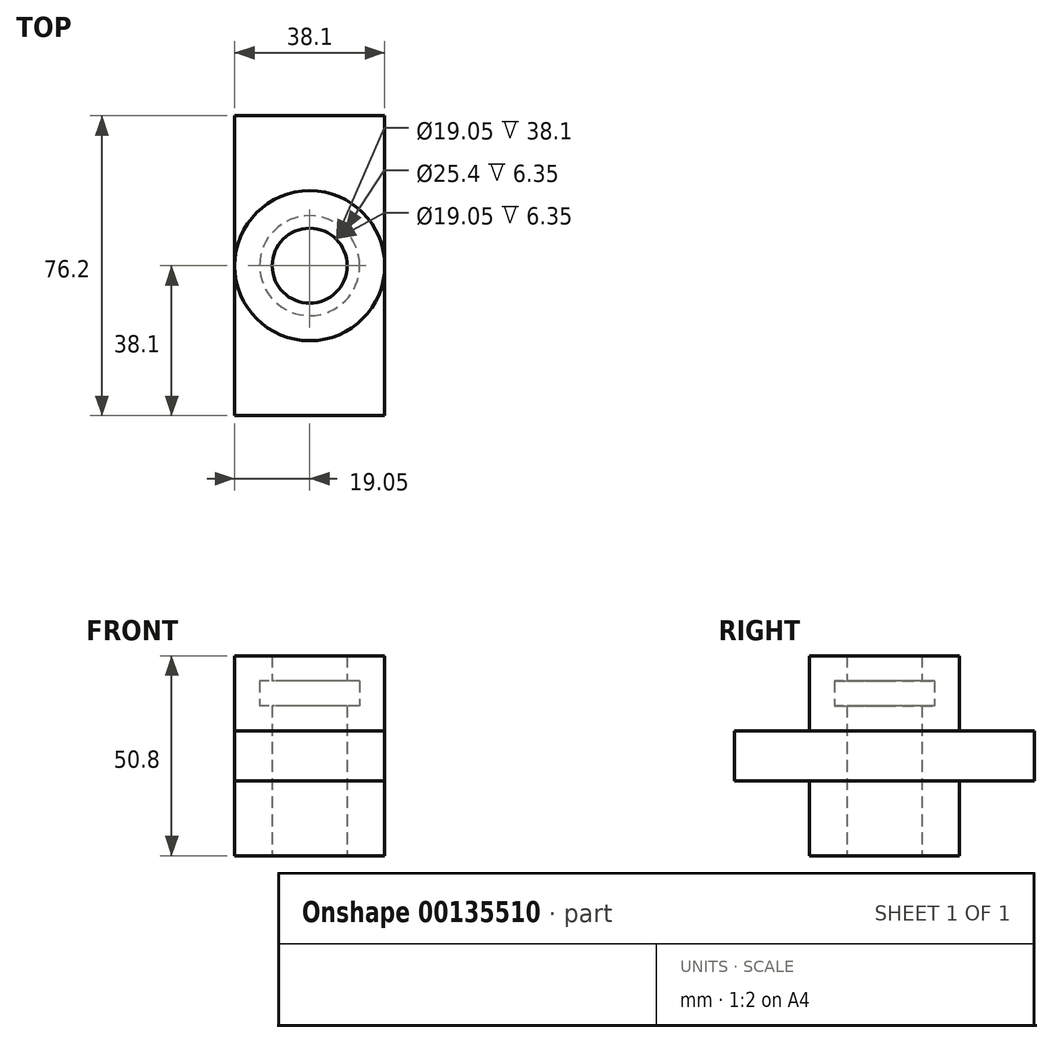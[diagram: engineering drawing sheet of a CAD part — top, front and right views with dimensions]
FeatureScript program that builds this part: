
annotation { "Feature Type Name" : "Feature", "Feature Type Description" : "" }
export const myFeature = defineFeature(function(context is Context, id is Id, definition is map)
    precondition{}
    {
        {
            var Q0;
            Q0=qCreatedBy(makeId("Top.planeOp"),FACE);
            var sketch = newSketch(context, id + "F0", { "sketchPlane" : qUnion([Q0])});
            skCircle(sketch, "E0", {"center": v(0, 0) * mm, "radius": 19.05 * mm});
            skCircle(sketch, "E1", {"center": v(0, 0) * mm, "radius": 9.53 * mm});
            skSolve(sketch);
        }
        {
            var Q0;
            Q0 = qSketchRegion(id + "F0", true);
            extrude(context, id + "F1", {"entities" : qUnion([Q0]), "depth" : 38.1 * mm});
        }
        {
            var Q0;
            Q0=makeQuery(id+"F1.opExtrude","CAP_FACE",FACE,{"disambiguationData":[OSD([sQuery(id+"F0.wireOp",EDGE,"E0"),sQuery(id+"F0.wireOp",EDGE,"E1")])],"isStart":false});
            var sketch = newSketch(context, id + "F2", { "sketchPlane" : qUnion([Q0])});
            skCircle(sketch, "E2.0", {"center": v(0, 0) * mm, "radius": 19.05 * mm});
            skCircle(sketch, "E3", {"center": v(0, 0) * mm, "radius": 12.7 * mm});
            skSolve(sketch);
        }
        {
            var Q0;
            Q0 = qSketchRegion(id + "F2", true);
            extrude(context, id + "F3", {"entities" : qUnion([Q0]), "operationType" : NewBodyOperationType.ADD, "depth" : 6.35 * mm});
        }
        {
            var Q0;
            Q0=makeQuery(id+"F3.opExtrude","CAP_FACE",FACE,{"disambiguationData":[OSD([sQuery(id+"F2.wireOp",EDGE,"E2.0"),sQuery(id+"F2.wireOp",EDGE,"E3")])],"isStart":false});
            var sketch = newSketch(context, id + "F4", { "sketchPlane" : qUnion([Q0])});
            skCircle(sketch, "E4.0", {"center": v(0, 0) * mm, "radius": 9.53 * mm});
            skCircle(sketch, "E4.1", {"center": v(0, 0) * mm, "radius": 19.05 * mm});
            skSolve(sketch);
        }
        {
            var Q0;
            Q0 = qSketchRegion(id + "F4", true);
            extrude(context, id + "F5", {"entities" : qUnion([Q0]), "operationType" : NewBodyOperationType.ADD, "depth" : 6.35 * mm});
        }
        {
            var Q0;
            Q0=qCreatedBy(makeId("Right.planeOp"),FACE);
            var sketch = newSketch(context, id + "F6", { "sketchPlane" : qUnion([Q0])});
            skLineSegment(sketch, "E5.bottom", {"start": v(-38.1, 19.05) * mm, "end": v(38.1, 19.05) * mm});
            skLineSegment(sketch, "E5.top", {"start": v(-38.1, 31.75) * mm, "end": v(38.1, 31.75) * mm});
            skLineSegment(sketch, "E5.left", {"start": v(-38.1, 19.05) * mm, "end": v(-38.1, 31.75) * mm});
            skLineSegment(sketch, "E5.right", {"start": v(38.1, 19.05) * mm, "end": v(38.1, 31.75) * mm});
            skPoint(sketch, "E5.middle", {"position": v(0, 25.4) * mm});
            skSolve(sketch);
        }
        {
            var Q0;
            Q0 = qSketchRegion(id + "F6", true);
            extrude(context, id + "F7", {"entities" : qUnion([Q0]), "operationType" : NewBodyOperationType.ADD, "endBound" : BoundingType.SYMMETRIC, "depth" : 38.1 * mm});
        }
        {
            var Q0;
            Q0=makeQuery(id+"F7.boolean.opBoolean","SPLIT",FACE,{"disambiguationData":[TD([makeQuery(id+"F1.opExtrude","SWEPT_FACE",FACE,{"disambiguationData":[OSD([sQuery(id+"F0.wireOp",EDGE,"E1")])]})])],"derivedFrom":makeQuery(id+"F7.opExtrude","SWEPT_FACE",FACE,{"disambiguationData":[OSD([sQuery(id+"F6.wireOp",EDGE,"E5.top")])]})});
            extrude(context, id + "F8", {"entities" : qUnion([Q0]), "operationType" : NewBodyOperationType.REMOVE, "endBound" : BoundingType.THROUGH_ALL, "oppositeDirection" : true, "depth" : 25.4 * mm, "hasSecondDirection" : true, "secondDirectionBound" : SecondDirectionBoundingType.THROUGH_ALL, "secondDirectionOppositeDirection" : false, "secondDirectionDepth" : 25.4 * mm});
        }
    });
